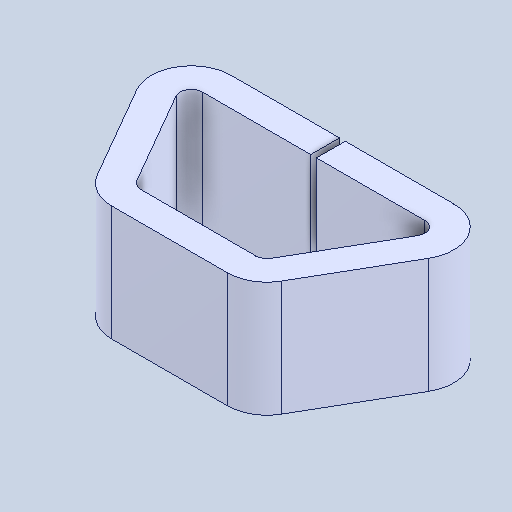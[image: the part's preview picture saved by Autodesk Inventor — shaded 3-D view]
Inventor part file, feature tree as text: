
AUTODESK INVENTOR PART (.ipt)
format: ipt  version: 2025 (Build 290162000, 162)  size: 107,008 bytes
history: native  units: mm
features: mirror x1
ambient origin geometry x8: Origin, YZ Plane, XZ Plane, XY Plane, X Axis, Y Axis, Z Axis, Center Point
bodies: Solid1 (feature_tree)
feature tree (1):
  mirror  "Mirror1"
